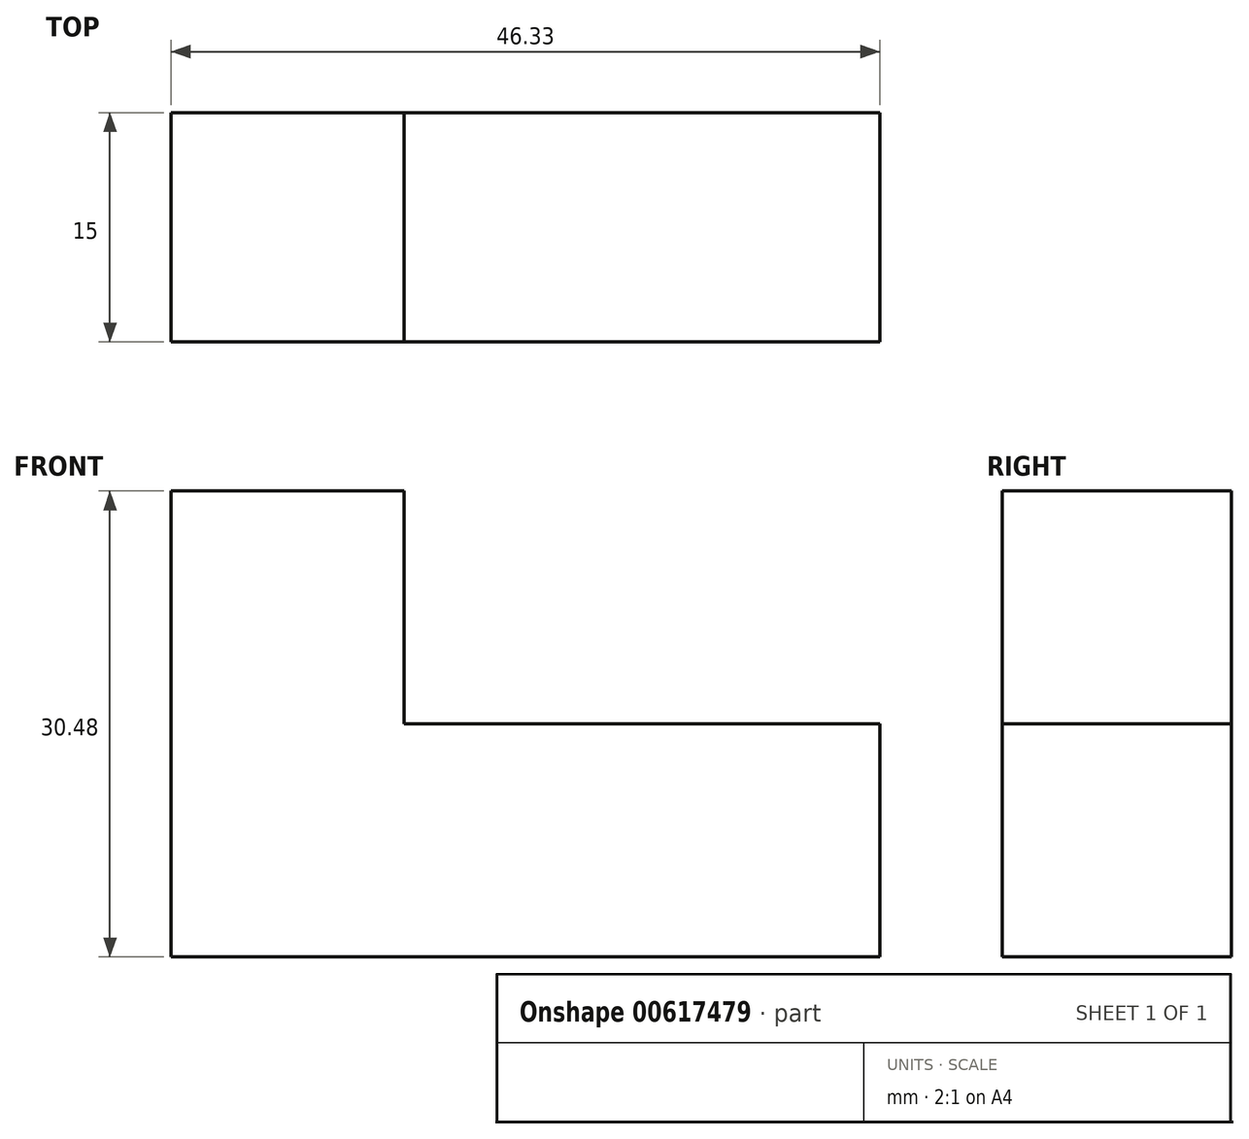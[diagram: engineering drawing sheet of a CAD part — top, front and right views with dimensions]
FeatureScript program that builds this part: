
annotation { "Feature Type Name" : "Feature", "Feature Type Description" : "" }
export const myFeature = defineFeature(function(context is Context, id is Id, definition is map)
    precondition{}
    {
        {
            var Q0;
            Q0=qCreatedBy(makeId("Front.planeOp"),FACE);
            var sketch = newSketch(context, id + "F0", { "sketchPlane" : qUnion([Q0])});
            skLineSegment(sketch, "E0", {"start": v(-59.9, 0) * mm, "end": v(-59.9, 15.24) * mm});
            skLineSegment(sketch, "E1", {"start": v(-59.9, 15.24) * mm, "end": v(-59.9, 30.48) * mm});
            skLineSegment(sketch, "E2", {"start": v(-59.9, 30.48) * mm, "end": v(-44.65, 30.48) * mm});
            skLineSegment(sketch, "E3", {"start": v(-44.65, 30.48) * mm, "end": v(-44.65, 15.24) * mm});
            skLineSegment(sketch, "E4", {"start": v(-44.65, 15.24) * mm, "end": v(-28.8, 15.24) * mm});
            skLineSegment(sketch, "E5", {"start": v(-28.8, 15.24) * mm, "end": v(-13.56, 15.24) * mm});
            skLineSegment(sketch, "E6", {"start": v(-13.56, 15.24) * mm, "end": v(-13.56, 0) * mm});
            skLineSegment(sketch, "E7", {"start": v(-59.9, 0) * mm, "end": v(-13.56, 0) * mm});
            skSolve(sketch);
        }
        {
            var Q0;
            Q0 = qSketchRegion(id + "F0", true);
            extrude(context, id + "F1", {"entities" : qUnion([Q0]), "depth" : 15 * mm, "offsetDistance" : 25.4 * mm});
        }
    });
